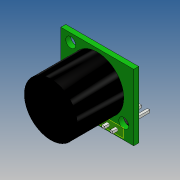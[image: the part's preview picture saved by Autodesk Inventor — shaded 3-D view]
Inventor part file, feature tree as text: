
AUTODESK INVENTOR PART (.ipt)
format: ipt  version: 2017 (Build 210142000, 142)  size: 311,296 bytes
history: native  units: mm
features: other x6, pattern_linear x2, extrude x2, plane x1, sketch x1
ambient origin geometry x8: Origin, YZ Plane, XZ Plane, XY Plane, X Axis, Y Axis, Z Axis, Center Point
bodies: Body1 (feature_tree), Body2 (feature_tree), Body3 (feature_tree)
feature tree (12):
  other  "2pin_header__02.ipt"
  pattern_linear  "Patrón rectangular1"  Count1=3 Spacing1=5.0mm
  pattern_linear  "Patrón rectangular2"  Count1=2 Spacing1=2.5mm
  plane  "Plano de trabajo1"
  sketch  "Boceto1"  dims[d0=10.0mm d1=30.0mm d3=5.0mm d4=20.0mm d6=2.5mm d7=16.0mm d8=22.0mm d9=20.0mm d10=6.857295mm d11=3.0mm d12=11.0mm d15=1.5mm d16=0.5mm d17=0.5mm d18=1.5mm d19=0.0mm d20=14.0mm d21=0.0mm]
  extrude  "Extrusión1"  Depth=14.0mm
  extrude  "Extrusión2"  Depth=22.0mm
  other  "Solid1::2pin_header__02.ipt"
  other  "OperaciónIdentificador1"
  other  "Sólido2"
  other  "Sólido3"
  other  "Sólido1"
